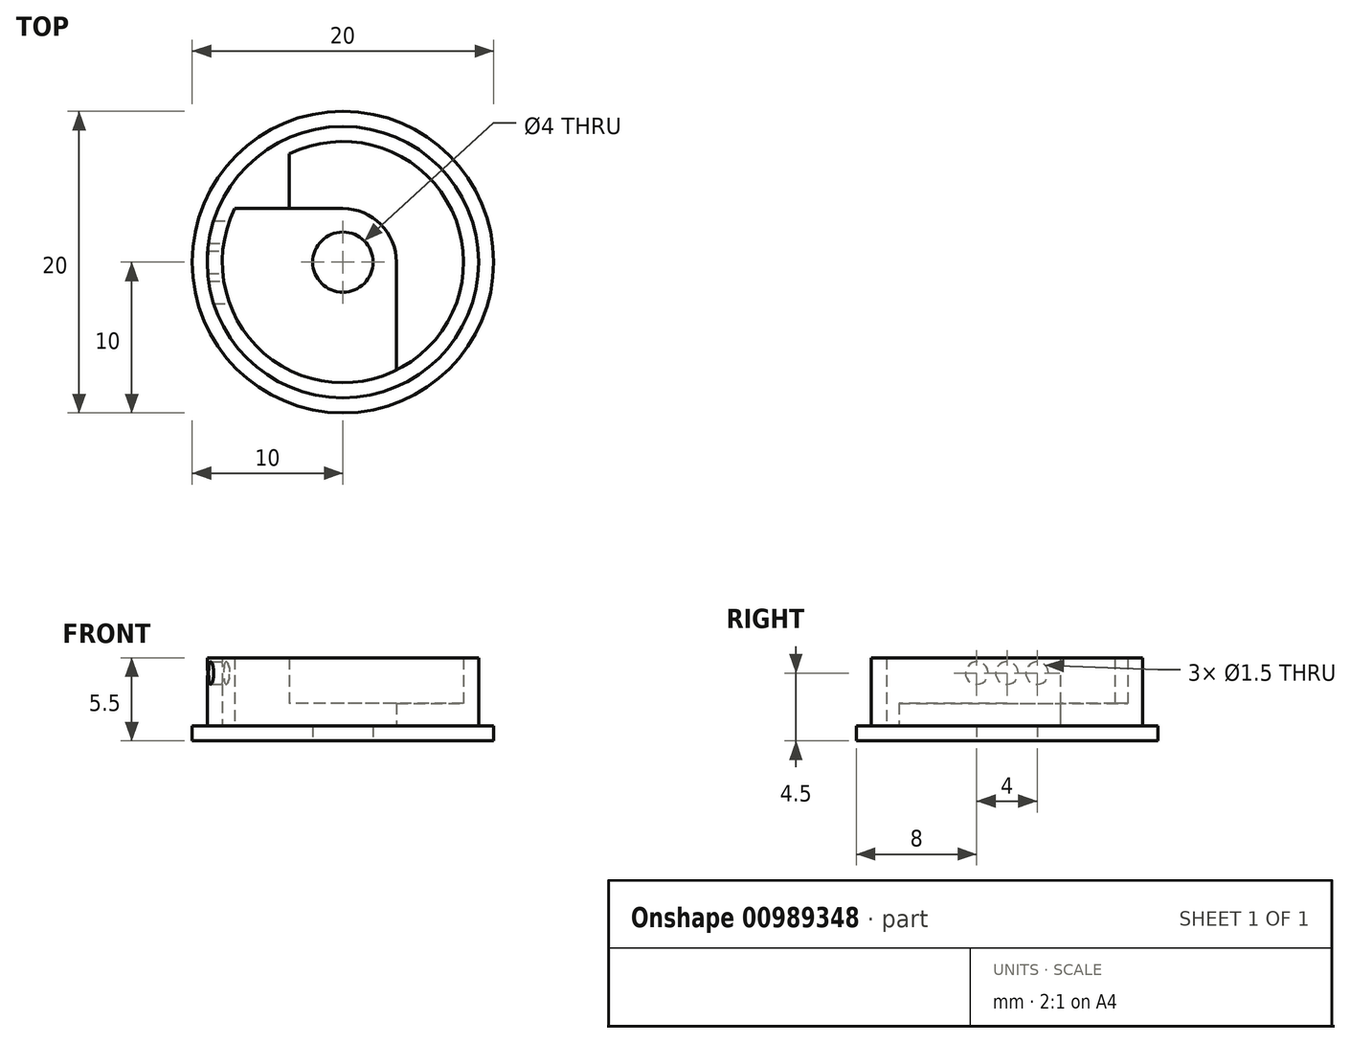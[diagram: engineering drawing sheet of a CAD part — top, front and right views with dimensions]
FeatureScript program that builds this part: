
annotation { "Feature Type Name" : "Feature", "Feature Type Description" : "" }
export const myFeature = defineFeature(function(context is Context, id is Id, definition is map)
    precondition{}
    {
        {
            var Q0;
            Q0=qCreatedBy(makeId("Top.planeOp"),FACE);
            var sketch = newSketch(context, id + "F0", { "sketchPlane" : qUnion([Q0])});
            skCircle(sketch, "E0", {"center": v(0, 0) * mm, "radius": 2 * mm});
            skCircle(sketch, "E1", {"center": v(0, 0) * mm, "radius": 9 * mm});
            skCircle(sketch, "E2", {"center": v(0, 0) * mm, "radius": 8 * mm});
            skCircle(sketch, "E3", {"center": v(0, 0) * mm, "radius": 10 * mm});
            skSolve(sketch);
        }
        {
            var Q0;
            Q0=makeQuery(id+"F0.imprint","IMPRINT",FACE,{"disambiguationData":[TD([[makeQuery(id+"F0.imprint","IMPRINT",EDGE,{"derivedFrom":sQuery(id+"F0.wireOp",EDGE,"E1")}),1.0]])]});
            var Q1;
            Q1=makeQuery(id+"F0.imprint","IMPRINT",FACE,{"disambiguationData":[TD([[makeQuery(id+"F0.imprint","IMPRINT",EDGE,{"derivedFrom":sQuery(id+"F0.wireOp",EDGE,"E0")}),-1.0]])]});
            var Q2;
            Q2=makeQuery(id+"F0.imprint","IMPRINT",FACE,{"disambiguationData":[TD([[makeQuery(id+"F0.imprint","IMPRINT",EDGE,{"derivedFrom":sQuery(id+"F0.wireOp",EDGE,"E1")}),-1.0]])]});
            extrude(context, id + "F1", {"entities" : qUnion([Q0, Q1, Q2]), "depth" : 1 * mm, "offsetDistance" : 25 * mm});
        }
        {
            var Q0;
            Q0=makeQuery(id+"F0.imprint","IMPRINT",FACE,{"disambiguationData":[TD([[makeQuery(id+"F0.imprint","IMPRINT",EDGE,{"derivedFrom":sQuery(id+"F0.wireOp",EDGE,"E1")}),1.0]])]});
            extrude(context, id + "F2", {"entities" : qUnion([Q0]), "operationType" : NewBodyOperationType.ADD, "depth" : 5.5 * mm, "offsetDistance" : 25 * mm});
        }
        {
            var Q0;
            {var subQ0=sQuery(id+"F0.wireOp",EDGE,"E0");Q0=makeQuery(id+"F2.boolean.opBoolean","SPLIT",FACE,{"disambiguationData":[TD([makeQuery(id+"F1.opExtrude","SWEPT_FACE",FACE,{"disambiguationData":[OSD([subQ0])]})])],"derivedFrom":makeQuery(id+"F1.opExtrude","CAP_FACE",FACE,{"disambiguationData":[OSD([subQ0,sQuery(id+"F0.wireOp",EDGE,"E3")])],"isStart":false})});}
            var sketch = newSketch(context, id + "F3", { "sketchPlane" : qUnion([Q0])});
            skLineSegment(sketch, "E4", {"start": v(0, 8) * mm, "end": v(0, -8) * mm});
            skCircle(sketch, "E5", {"center": v(0, 0) * mm, "radius": 3.55 * mm});
            skLineSegment(sketch, "E6", {"start": v(3.55, 0) * mm, "end": v(3.55, -7.17) * mm});
            skLineSegment(sketch, "E7", {"start": v(-3.55, 0) * mm, "end": v(-3.55, 7.17) * mm});
            skLineSegment(sketch, "E8", {"start": v(0, 3.55) * mm, "end": v(-7.17, 3.55) * mm});
            skSolve(sketch);
        }
        {
            var Q0;
            {var subQ0=sQuery(id+"F3.wireOp",EDGE,"E6");Q0=makeQuery(id+"F3.imprint","IMPRINT",FACE,{"disambiguationData":[TD([[makeQuery(id+"F3.imprint","IMPRINT",EDGE,{"derivedFrom":subQ0}),1.0]])]});}
            var Q1;
            {var subQ3=sQuery(id+"F3.wireOp",EDGE,"NPgIKNHn-BGVs-yLH1-UR2K-JrwnbXS1szmv");Q1=makeQuery(id+"F3.imprint","IMPRINT",FACE,{"disambiguationData":[TD([[makeQuery(id+"F3.imprint","IMPRINT",EDGE,{"derivedFrom":subQ3}),-1.0]])]});}
            var Q2;
            {var subQ3=sQuery(id+"F3.wireOp",EDGE,"NPgIKNHn-BGVs-yLH1-UR2K-JrwnbXS1szmv");var subQ5=sQuery(id+"F3.wireOp",EDGE,"E7");var subQ6=makeQuery(id+"F3.imprint","INTERSECT",VERTEX,{"derivedFrom":[subQ3,subQ5]});Q2=makeQuery(id+"F3.imprint","IMPRINT",FACE,{"disambiguationData":[TD([[makeQuery(id+"F3.imprint","IMPRINT",EDGE,{"disambiguationData":[TD([[subQ6,1.0]])],"derivedFrom":subQ3}),-1.0]])]});}
            var Q3;
            {var subQ3=sQuery(id+"F3.wireOp",EDGE,"E8");var subQ5=sQuery(id+"F3.wireOp",EDGE,"E7");var subQ7=makeQuery(id+"F3.imprint","INTERSECT",VERTEX,{"derivedFrom":[subQ5,subQ3]});Q3=makeQuery(id+"F3.imprint","IMPRINT",FACE,{"disambiguationData":[TD([[makeQuery(id+"F3.imprint","IMPRINT",EDGE,{"disambiguationData":[TD([[subQ7,1.0]])],"derivedFrom":subQ3}),-1.0]])]});}
            var Q4;
            {var subQ0=sQuery(id+"F3.wireOp",EDGE,"E7");var subQ3=sQuery(id+"F3.wireOp",EDGE,"E8");var subQ4=makeQuery(id+"F3.imprint","INTERSECT",VERTEX,{"derivedFrom":[subQ0,subQ3]});Q4=makeQuery(id+"F3.imprint","IMPRINT",FACE,{"disambiguationData":[TD([[makeQuery(id+"F3.imprint","IMPRINT",EDGE,{"disambiguationData":[TD([[subQ4,-1.0]])],"derivedFrom":subQ0}),1.0]])]});}
            extrude(context, id + "F4", {"entities" : qUnion([Q0, Q1, Q2, Q3, Q4]), "operationType" : NewBodyOperationType.ADD, "depth" : 1.5 * mm, "offsetDistance" : 25 * mm});
        }
        {
            var Q0;
            {var subQ0=sQuery(id+"F3.wireOp",EDGE,"E7");var subQ3=sQuery(id+"F3.wireOp",EDGE,"E8");var subQ4=makeQuery(id+"F3.imprint","INTERSECT",VERTEX,{"derivedFrom":[subQ0,subQ3]});Q0=makeQuery(id+"F3.imprint","IMPRINT",FACE,{"disambiguationData":[TD([[makeQuery(id+"F3.imprint","IMPRINT",EDGE,{"disambiguationData":[TD([[subQ4,-1.0]])],"derivedFrom":subQ0}),1.0]])]});}
            extrude(context, id + "F5", {"entities" : qUnion([Q0]), "operationType" : NewBodyOperationType.ADD, "depth" : 4.5 * mm, "offsetDistance" : 25 * mm});
        }
        {
            var Q0;
            Q0=qCreatedBy(makeId("Right.planeOp"),FACE);
            var sketch = newSketch(context, id + "F6", { "sketchPlane" : qUnion([Q0])});
            skLineSegment(sketch, "E9", {"start": v(0, 0) * mm, "end": v(0, 4.5) * mm});
            skLineSegment(sketch, "E10", {"start": v(0, 4.5) * mm, "end": v(2, 4.5) * mm});
            skCircle(sketch, "E11", {"center": v(2, 4.5) * mm, "radius": 0.75 * mm});
            skCircle(sketch, "E12", {"center": v(0, 4.5) * mm, "radius": 0.75 * mm});
            skLineSegment(sketch, "E13", {"start": v(0, 4.5) * mm, "end": v(-2, 4.5) * mm});
            skCircle(sketch, "E14", {"center": v(-2, 4.5) * mm, "radius": 0.75 * mm});
            skSolve(sketch);
        }
        {
            var Q0;
            {var subQ1=sQuery(id+"F6.wireOp",EDGE,"E9");var subQ3=sQuery(id+"F6.wireOp",EDGE,"E12");var subQ4=makeQuery(id+"F6.imprint","INTERSECT",VERTEX,{"derivedFrom":[subQ1,subQ3]});Q0=makeQuery(id+"F6.imprint","IMPRINT",FACE,{"disambiguationData":[TD([[makeQuery(id+"F6.imprint","IMPRINT",EDGE,{"disambiguationData":[TD([[subQ4,-1.0]])],"derivedFrom":subQ3}),1.0]])]});}
            var Q1;
            {var subQ1=sQuery(id+"F6.wireOp",EDGE,"E10");var subQ3=sQuery(id+"F6.wireOp",EDGE,"E12");var subQ4=makeQuery(id+"F6.imprint","INTERSECT",VERTEX,{"derivedFrom":[subQ1,subQ3]});Q1=makeQuery(id+"F6.imprint","IMPRINT",FACE,{"disambiguationData":[TD([[makeQuery(id+"F6.imprint","IMPRINT",EDGE,{"disambiguationData":[TD([[subQ4,-1.0]])],"derivedFrom":subQ3}),1.0]])]});}
            var Q2;
            {var subQ1=sQuery(id+"F6.wireOp",EDGE,"E9");var subQ3=sQuery(id+"F6.wireOp",EDGE,"E12");var subQ4=makeQuery(id+"F6.imprint","INTERSECT",VERTEX,{"derivedFrom":[subQ1,subQ3]});Q2=makeQuery(id+"F6.imprint","IMPRINT",FACE,{"disambiguationData":[TD([[makeQuery(id+"F6.imprint","IMPRINT",EDGE,{"disambiguationData":[TD([[subQ4,1.0]])],"derivedFrom":subQ3}),1.0]])]});}
            var Q3;
            Q3=makeQuery(id+"F6.imprint","IMPRINT",FACE,{"disambiguationData":[TD([[makeQuery(id+"F6.imprint","IMPRINT",EDGE,{"derivedFrom":sQuery(id+"F6.wireOp",EDGE,"E14")}),1.0]])]});
            var Q4;
            Q4=makeQuery(id+"F6.imprint","IMPRINT",FACE,{"disambiguationData":[TD([[makeQuery(id+"F6.imprint","IMPRINT",EDGE,{"derivedFrom":sQuery(id+"F6.wireOp",EDGE,"E11")}),1.0]])]});
            var Q5;
            Q5=makeQuery(id+"F2.opExtrude","SWEPT_FACE",FACE,{"disambiguationData":[OSD([sQuery(id+"F0.wireOp",EDGE,"E1")])]});
            var Q6;
            Q6=makeQuery(id+"F2.opExtrude","SWEPT_FACE",FACE,{"disambiguationData":[OSD([sQuery(id+"F0.wireOp",EDGE,"E2")])]});
            extrude(context, id + "F7", {"entities" : qUnion([Q0, Q1, Q2, Q3, Q4]), "operationType" : NewBodyOperationType.REMOVE, "endBound" : BoundingType.UP_TO_SURFACE, "oppositeDirection" : true, "depth" : 25 * mm, "endBoundEntityFace" : qUnion([Q5]), "offsetDistance" : 25 * mm, "hasSecondDirection" : true, "secondDirectionBound" : SecondDirectionBoundingType.UP_TO_SURFACE, "secondDirectionOppositeDirection" : false, "secondDirectionDepth" : 25 * mm, "secondDirectionBoundEntityFace" : qUnion([Q6])});
        }
    });
